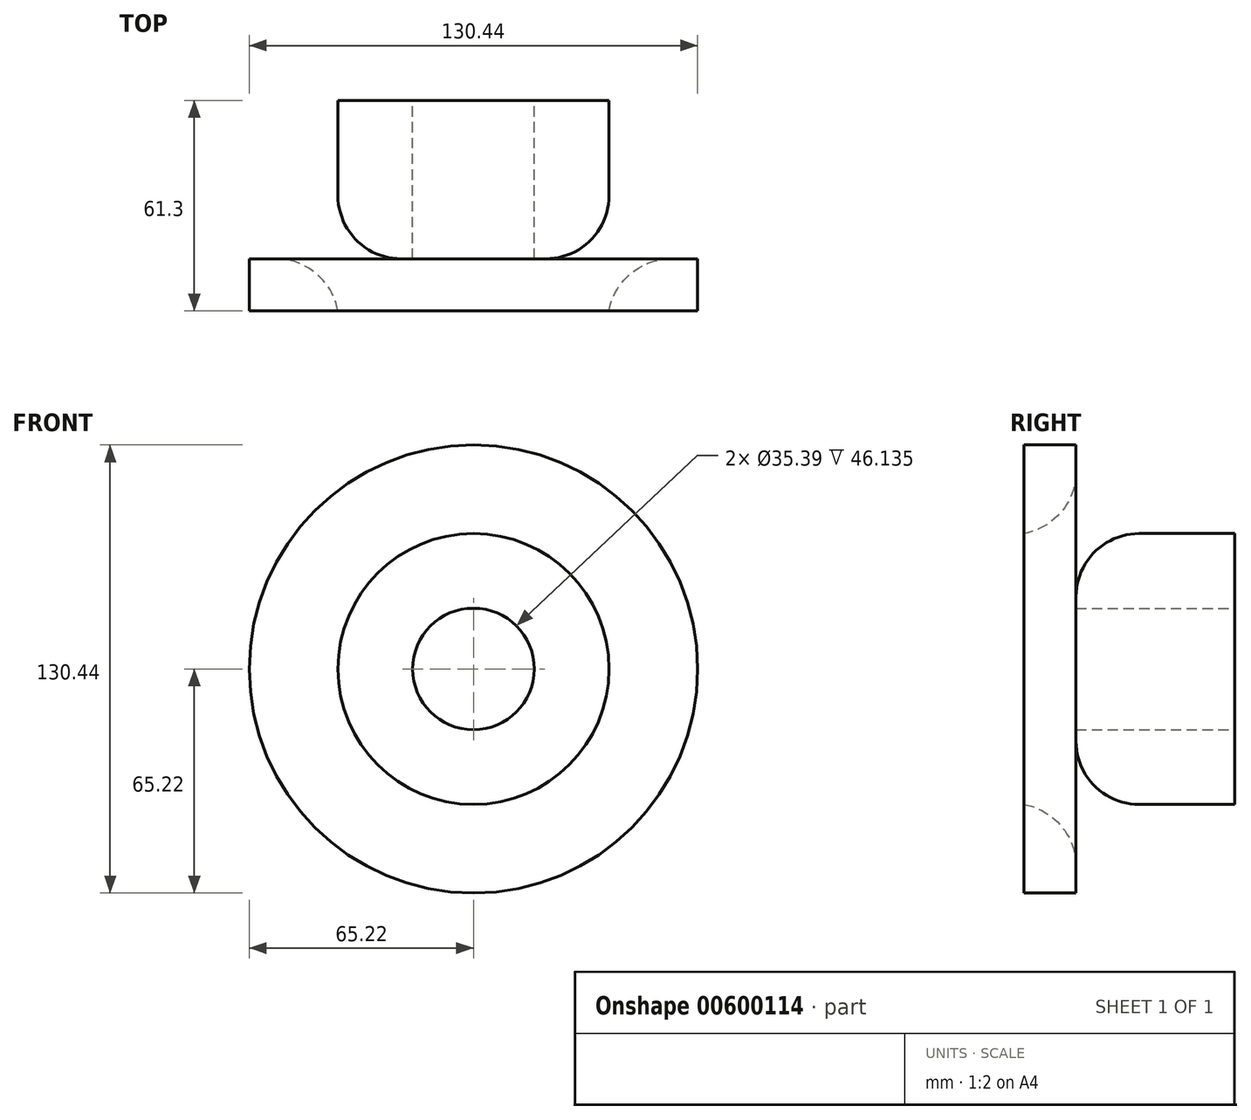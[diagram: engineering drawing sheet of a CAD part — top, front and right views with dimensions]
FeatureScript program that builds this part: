
annotation { "Feature Type Name" : "Feature", "Feature Type Description" : "" }
export const myFeature = defineFeature(function(context is Context, id is Id, definition is map)
    precondition{}
    {
        {
            var Q0;
            Q0=qCreatedBy(makeId("Right.planeOp"),FACE);
            var sketch = newSketch(context, id + "F0", { "sketchPlane" : qUnion([Q0])});
            skLineSegment(sketch, "E0.bottom", {"start": v(-61.3, 17.7) * mm, "end": v(-46.14, 17.7) * mm});
            skLineSegment(sketch, "E0.top", {"start": v(-61.3, 65.22) * mm, "end": v(-46.14, 65.22) * mm});
            skLineSegment(sketch, "E0.left", {"start": v(-61.3, 17.7) * mm, "end": v(-61.3, 65.22) * mm});
            skLineSegment(sketch, "E0.right", {"start": v(-46.14, 17.7) * mm, "end": v(-46.14, 65.22) * mm});
            skLineSegment(sketch, "E1.bottom", {"start": v(-61.3, 17.7) * mm, "end": v(0, 17.7) * mm});
            skLineSegment(sketch, "E1.top", {"start": v(-61.3, 39.44) * mm, "end": v(0, 39.44) * mm});
            skLineSegment(sketch, "E1.left", {"start": v(-61.3, 17.7) * mm, "end": v(-61.3, 39.44) * mm});
            skLineSegment(sketch, "E1.right", {"start": v(0, 17.7) * mm, "end": v(0, 39.44) * mm});
            skLineSegment(sketch, "E2.MirrorCS", {"start": v(-61.3, -17.7) * mm, "end": v(-46.14, -17.7) * mm});
            skLineSegment(sketch, "E3.MirrorCS", {"start": v(-61.3, -39.44) * mm, "end": v(0, -39.44) * mm});
            skLineSegment(sketch, "E4.MirrorCS", {"start": v(-61.3, -65.22) * mm, "end": v(-46.14, -65.22) * mm});
            skLineSegment(sketch, "E5.MirrorCS", {"start": v(-61.3, -17.7) * mm, "end": v(-61.3, -65.22) * mm});
            skLineSegment(sketch, "E6.MirrorCS", {"start": v(-61.3, -17.7) * mm, "end": v(-61.3, -39.44) * mm});
            skLineSegment(sketch, "E7.MirrorCS", {"start": v(-61.3, -17.7) * mm, "end": v(0, -17.7) * mm});
            skLineSegment(sketch, "E8.MirrorCS", {"start": v(0, -17.7) * mm, "end": v(0, -39.44) * mm});
            skLineSegment(sketch, "E9.MirrorCS", {"start": v(-46.14, -17.7) * mm, "end": v(-46.14, -65.22) * mm});
            skLineSegment(sketch, "E10", {"start": v(0, 0) * mm, "end": v(-61.3, 0) * mm});
            skSolve(sketch);
        }
        {
            var Q0;
            {var subQ0=sQuery(id+"F0.wireOp",EDGE,"E0.top");Q0=makeQuery(id+"F0.imprint","IMPRINT",FACE,{"disambiguationData":[TD([[makeQuery(id+"F0.imprint","IMPRINT",EDGE,{"derivedFrom":subQ0}),-1.0]])]});}
            var Q1;
            {var subQ5=sQuery(id+"F0.wireOp",EDGE,"E1.left");Q1=makeQuery(id+"F0.imprint","IMPRINT",FACE,{"disambiguationData":[TD([[makeQuery(id+"F0.imprint","IMPRINT",EDGE,{"derivedFrom":subQ5}),-1.0]])]});}
            var Q2;
            {var subQ5=sQuery(id+"F0.wireOp",EDGE,"E1.right");Q2=makeQuery(id+"F0.imprint","IMPRINT",FACE,{"disambiguationData":[TD([[makeQuery(id+"F0.imprint","IMPRINT",EDGE,{"derivedFrom":subQ5}),1.0]])]});}
            var Q3;
            Q3=sQuery(id+"F0.wireOp",EDGE,"E10");
            revolve(context, id + "F1", {"entities" : qUnion([Q0, Q1, Q2]), "axis" : qUnion([Q3]), "revolveType" : RevolveType.FULL});
        }
        {
            var Q0;
            Q0=makeQuery(id+"F1.opRevolve","SWEPT_EDGE",EDGE,{"disambiguationData":[OSD([sQuery(id+"F0.wireOp",EDGE,"E0.right"),sQuery(id+"F0.wireOp",EDGE,"E1.top")])]});
            fillet(context, id + "F2", {"entities" : qUnion([Q0]), "radius" : 18.4 * mm, "tangentPropagation" : true, "allowEdgeOverflow" : false});
        }
    });
